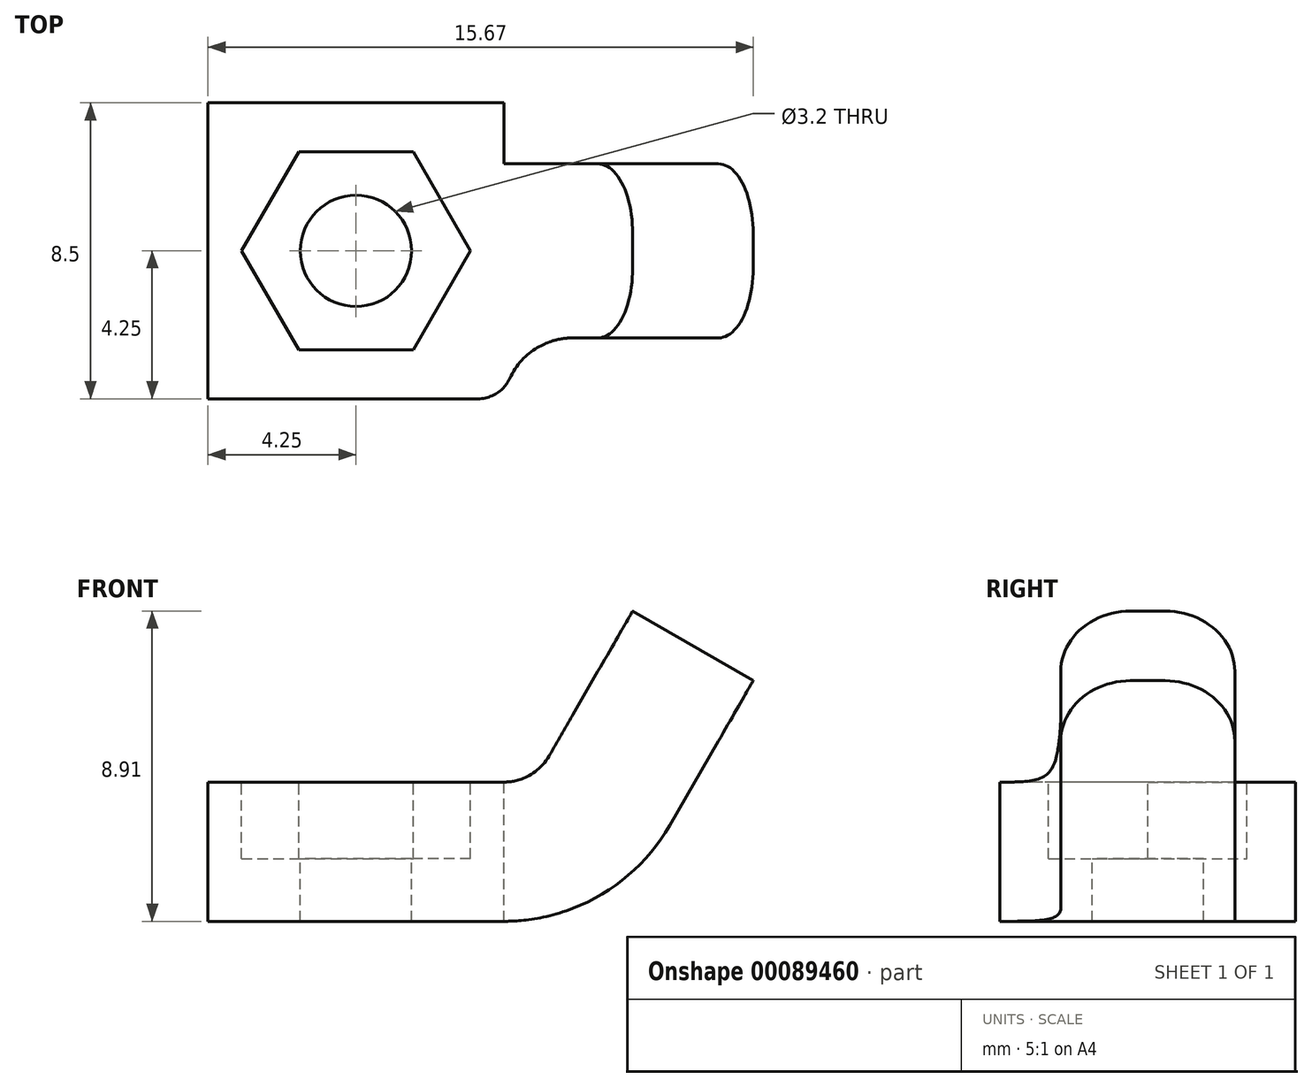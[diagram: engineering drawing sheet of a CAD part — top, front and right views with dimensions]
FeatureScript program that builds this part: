
annotation { "Feature Type Name" : "Feature", "Feature Type Description" : "" }
export const myFeature = defineFeature(function(context is Context, id is Id, definition is map)
    precondition{}
    {
        {
            var Q0;
            Q0=qCreatedBy(makeId("Top.planeOp"),FACE);
            var sketch = newSketch(context, id + "F0", { "sketchPlane" : qUnion([Q0])});
            skLineSegment(sketch, "E0.bottom", {"start": v(4.25, 4.25) * mm, "end": v(-4.25, 4.25) * mm});
            skLineSegment(sketch, "E0.top", {"start": v(4.25, -4.25) * mm, "end": v(-4.25, -4.25) * mm});
            skLineSegment(sketch, "E0.left", {"start": v(4.25, 4.25) * mm, "end": v(4.25, -4.25) * mm});
            skLineSegment(sketch, "E0.right", {"start": v(-4.25, 4.25) * mm, "end": v(-4.25, -4.25) * mm});
            skPoint(sketch, "E1", {"position": v(0, 0) * mm});
            skPoint(sketch, "E2", {"position": v(0, 4.25) * mm});
            skPoint(sketch, "E3", {"position": v(-4.25, 0) * mm});
            skCircle(sketch, "E4.cCircle", {"center": v(0, 0) * mm, "radius": 2.75 * mm, "construction": true});
            skLineSegment(sketch, "E4.0", {"start": v(-1.59, 2.75) * mm, "end": v(1.59, 2.75) * mm});
            skLineSegment(sketch, "E4.1", {"start": v(1.59, 2.75) * mm, "end": v(3.18, 0) * mm});
            skLineSegment(sketch, "E4.2", {"start": v(3.18, 0) * mm, "end": v(1.59, -2.75) * mm});
            skLineSegment(sketch, "E4.3", {"start": v(1.59, -2.75) * mm, "end": v(-1.59, -2.75) * mm});
            skLineSegment(sketch, "E4.4", {"start": v(-1.59, -2.75) * mm, "end": v(-3.18, 0) * mm});
            skLineSegment(sketch, "E4.5", {"start": v(-3.18, 0) * mm, "end": v(-1.59, 2.75) * mm});
            skPoint(sketch, "E4.0.midPoint", {"position": v(0, 2.75) * mm});
            skSolve(sketch);
        }
        {
            var Q0;
            Q0=qSketchRegion(id+"F0",true);
            var Q1;
            Q1=makeQuery(id+"F0.imprint","IMPRINT",FACE,{"disambiguationData":[TD([[makeQuery(id+"F0.imprint","IMPRINT",EDGE,{"derivedFrom":sQuery(id+"F0.wireOp",EDGE,"9c3ea140-8654-4120-b5e6-7aedb879b978.0")}),-1.0]])]});
            var Q2;
            Q2=makeQuery(id+"F0.imprint","IMPRINT",FACE,{"disambiguationData":[TD([[makeQuery(id+"F0.imprint","IMPRINT",EDGE,{"derivedFrom":sQuery(id+"F0.wireOp",EDGE,"E4.0")}),-1.0]])]});
            extrude(context, id + "F1", {"entities" : qUnion([Q0, Q1, Q2]), "depth" : 4 * mm});
        }
        {
            var Q0;
            Q0=makeQuery(id+"F1.opExtrude","CAP_FACE",FACE,{"disambiguationData":[OSD([sQuery(id+"F0.wireOp",EDGE,"E0.bottom"),sQuery(id+"F0.wireOp",EDGE,"E0.top"),sQuery(id+"F0.wireOp",EDGE,"E0.left"),sQuery(id+"F0.wireOp",EDGE,"E0.right")])],"isStart":false});
            var sketch = newSketch(context, id + "F2", { "sketchPlane" : qUnion([Q0])});
            skCircle(sketch, "E5.cCircle", {"center": v(0, 0) * mm, "radius": 2.85 * mm, "construction": true});
            skLineSegment(sketch, "E5.0", {"start": v(-1.65, 2.85) * mm, "end": v(1.65, 2.85) * mm});
            skLineSegment(sketch, "E5.1", {"start": v(1.65, 2.85) * mm, "end": v(3.3, 0) * mm});
            skLineSegment(sketch, "E5.2", {"start": v(3.3, 0) * mm, "end": v(1.65, -2.85) * mm});
            skLineSegment(sketch, "E5.3", {"start": v(1.65, -2.85) * mm, "end": v(-1.65, -2.85) * mm});
            skLineSegment(sketch, "E5.4", {"start": v(-1.65, -2.85) * mm, "end": v(-3.3, 0) * mm});
            skLineSegment(sketch, "E5.5", {"start": v(-3.3, 0) * mm, "end": v(-1.65, 2.85) * mm});
            skPoint(sketch, "E5.0.midPoint", {"position": v(0, 2.85) * mm});
            skSolve(sketch);
        }
        {
            var Q0;
            Q0 = qSketchRegion(id + "F2", true);
            extrude(context, id + "F3", {"entities" : qUnion([Q0]), "operationType" : NewBodyOperationType.REMOVE, "oppositeDirection" : true, "depth" : 2.2 * mm});
        }
        {
            var Q0;
            Q0=makeQuery(id+"F3.boolean.opBoolean","COPY",FACE,{"derivedFrom":makeQuery(id+"F3.opExtrude","CAP_FACE",FACE,{"disambiguationData":[OSD([sQuery(id+"F2.wireOp",EDGE,"E5.0"),sQuery(id+"F2.wireOp",EDGE,"E5.1"),sQuery(id+"F2.wireOp",EDGE,"E5.2"),sQuery(id+"F2.wireOp",EDGE,"E5.3"),sQuery(id+"F2.wireOp",EDGE,"E5.4"),sQuery(id+"F2.wireOp",EDGE,"E5.5")])],"isStart":false})});
            var sketch = newSketch(context, id + "F4", { "sketchPlane" : qUnion([Q0])});
            skCircle(sketch, "E6", {"center": v(0, 0) * mm, "radius": 1.6 * mm});
            skSolve(sketch);
        }
        {
            var Q0;
            Q0 = qSketchRegion(id + "F4", true);
            extrude(context, id + "F5", {"entities" : qUnion([Q0]), "operationType" : NewBodyOperationType.REMOVE, "endBound" : BoundingType.THROUGH_ALL, "oppositeDirection" : true, "depth" : 25 * mm});
        }
        {
            var Q0;
            Q0=qCreatedBy(makeId("Front.planeOp"),FACE);
            var sketch = newSketch(context, id + "F6", { "sketchPlane" : qUnion([Q0])});
            skLineSegment(sketch, "E7", {"start": v(0, 0) * mm, "end": v(0, 5) * mm});
            skLineSegment(sketch, "E8", {"start": v(0, 2.5) * mm, "end": v(4.25, 2.5) * mm});
            skLineSegment(sketch, "E9", {"start": v(6.85, 4) * mm, "end": v(9.25, 8.16) * mm});
            skPoint(sketch, "E10.visualSharp", {"position": v(5.98, 2.5) * mm});
            skArc(sketch, "E10.filletArc", {"start": v(4.25, 2.5) * mm, "mid": v(5.75, 2.9) * mm, "end": v(6.85, 4) * mm});
            skArc(sketch, "E11.MirrorCS", {"start": v(-4.25, 2.5) * mm, "mid": v(-5.75, 2.9) * mm, "end": v(-6.85, 4) * mm});
            skLineSegment(sketch, "E12.MirrorCS", {"start": v(-6.85, 4) * mm, "end": v(-9.25, 8.16) * mm});
            skSolve(sketch);
        }
        {
            var Q0;
            Q0=makeQuery(id+"F1.opExtrude","SWEPT_FACE",FACE,{"disambiguationData":[OSD([sQuery(id+"F0.wireOp",EDGE,"E0.left")])]});
            var sketch = newSketch(context, id + "F7", { "sketchPlane" : qUnion([Q0])});
            skLineSegment(sketch, "E13.bottom", {"start": v(-2.5, 0) * mm, "end": v(2.5, 0) * mm});
            skLineSegment(sketch, "E13.top", {"start": v(-2.5, 4) * mm, "end": v(2.5, 4) * mm});
            skLineSegment(sketch, "E13.left", {"start": v(-2.5, 0) * mm, "end": v(-2.5, 4) * mm});
            skLineSegment(sketch, "E13.right", {"start": v(2.5, 0) * mm, "end": v(2.5, 4) * mm});
            skPoint(sketch, "E14", {"position": v(0, 0) * mm});
            skSolve(sketch);
        }
        {
            var Q0;
            Q0=makeQuery(id+"F7.imprint","IMPRINT",FACE,{"disambiguationData":[TD([[makeQuery(id+"F7.imprint","IMPRINT",EDGE,{"derivedFrom":sQuery(id+"F7.wireOp",EDGE,"E13.bottom")}),-1.0]])]});
            var Q1;
            Q1=sQuery(id+"F6.wireOp",EDGE,"E10.filletArc");
            var Q2;
            Q2=sQuery(id+"F6.wireOp",EDGE,"E9");
            sweep(context, id + "F8", {"operationType" : NewBodyOperationType.ADD, "profiles" : qUnion([Q0]), "path" : qUnion([Q1, Q2])});
        }
        {
            var Q0;
            Q0=makeQuery(id+"F8.opSweep","CAP_EDGE",EDGE,{"disambiguationData":[OSD([sQuery(id+"F6.wireOp",VERTEX,"E10.filletArc.start"),sQuery(id+"F7.wireOp",EDGE,"E13.left")])],"isStart":true});
            var Q1;
            Q1=makeQuery(id+"FKS6proBDLbqMdM_1.1.F8.opSweep","CAP_EDGE",EDGE,{"disambiguationData":[OSD([sQuery(id+"F6.wireOp",VERTEX,"E10.filletArc.start"),sQuery(id+"F7.wireOp",EDGE,"E13.right")])],"isStart":true});
            var Q2;
            Q2=makeQuery(id+"FKS6proBDLbqMdM_1.1.F8.opSweep","CAP_EDGE",EDGE,{"disambiguationData":[OSD([sQuery(id+"F6.wireOp",VERTEX,"E10.filletArc.start"),sQuery(id+"F7.wireOp",EDGE,"E13.left")])],"isStart":true});
            var Q3;
            Q3=makeQuery(id+"F8.opSweep","CAP_EDGE",EDGE,{"disambiguationData":[OSD([sQuery(id+"F6.wireOp",VERTEX,"E10.filletArc.start"),sQuery(id+"F7.wireOp",EDGE,"E13.right")])],"isStart":true});
            fillet(context, id + "F9", {"entities" : qUnion([Q0, Q1, Q2, Q3]), "radius" : 2 * mm, "tangentPropagation" : true, "allowEdgeOverflow" : false});
        }
        {
            var Q0;
            Q0=makeQuery(id+"FKS6proBDLbqMdM_1.1.F8.opSweep","CAP_EDGE",EDGE,{"disambiguationData":[OSD([sQuery(id+"F6.wireOp",VERTEX,"E9.end"),sQuery(id+"F7.wireOp",EDGE,"E13.left")])],"isStart":false});
            var Q1;
            Q1=makeQuery(id+"FKS6proBDLbqMdM_1.1.F8.opSweep","CAP_EDGE",EDGE,{"disambiguationData":[OSD([sQuery(id+"F6.wireOp",VERTEX,"E9.end"),sQuery(id+"F7.wireOp",EDGE,"E13.right")])],"isStart":false});
            var Q2;
            Q2=makeQuery(id+"F8.opSweep","CAP_EDGE",EDGE,{"disambiguationData":[OSD([sQuery(id+"F6.wireOp",VERTEX,"E9.end"),sQuery(id+"F7.wireOp",EDGE,"E13.right")])],"isStart":false});
            var Q3;
            Q3=makeQuery(id+"F8.opSweep","CAP_EDGE",EDGE,{"disambiguationData":[OSD([sQuery(id+"F6.wireOp",VERTEX,"E9.end"),sQuery(id+"F7.wireOp",EDGE,"E13.left")])],"isStart":false});
            fillet(context, id + "F10", {"entities" : qUnion([Q0, Q1, Q2, Q3]), "radius" : 2 * mm, "tangentPropagation" : true, "allowEdgeOverflow" : false});
        }
        {
            var Q0;
            Q0=makeQuery(id+"F9.opFillet","BLEND_EDGE",EDGE,{"blendedFrom":[makeQuery(id+"FKS6proBDLbqMdM_1.1.F8.opSweep","CAP_EDGE",EDGE,{"disambiguationData":[OSD([sQuery(id+"F6.wireOp",VERTEX,"E10.filletArc.start"),sQuery(id+"F7.wireOp",EDGE,"E13.left")])],"isStart":true}),makeQuery(id+"F1.opExtrude","SWEPT_FACE",FACE,{"disambiguationData":[OSD([sQuery(id+"F0.wireOp",EDGE,"E0.bottom")])]})],"blendedInto":[makeQuery(id+"F1.opExtrude","SWEPT_FACE",FACE,{"disambiguationData":[OSD([sQuery(id+"F0.wireOp",EDGE,"E0.bottom")])]})]});
            var Q1;
            Q1=makeQuery(id+"F9.opFillet","BLEND_EDGE",EDGE,{"blendedFrom":[makeQuery(id+"F8.opSweep","CAP_EDGE",EDGE,{"disambiguationData":[OSD([sQuery(id+"F6.wireOp",VERTEX,"E10.filletArc.start"),sQuery(id+"F7.wireOp",EDGE,"E13.right")])],"isStart":true}),makeQuery(id+"F1.opExtrude","SWEPT_FACE",FACE,{"disambiguationData":[OSD([sQuery(id+"F0.wireOp",EDGE,"E0.bottom")])]})],"blendedInto":[makeQuery(id+"F1.opExtrude","SWEPT_FACE",FACE,{"disambiguationData":[OSD([sQuery(id+"F0.wireOp",EDGE,"E0.bottom")])]})]});
            var Q2;
            Q2=makeQuery(id+"F9.opFillet","BLEND_EDGE",EDGE,{"blendedFrom":[makeQuery(id+"F8.opSweep","CAP_EDGE",EDGE,{"disambiguationData":[OSD([sQuery(id+"F6.wireOp",VERTEX,"E10.filletArc.start"),sQuery(id+"F7.wireOp",EDGE,"E13.left")])],"isStart":true}),makeQuery(id+"F1.opExtrude","SWEPT_FACE",FACE,{"disambiguationData":[OSD([sQuery(id+"F0.wireOp",EDGE,"E0.top")])]})],"blendedInto":[makeQuery(id+"F1.opExtrude","SWEPT_FACE",FACE,{"disambiguationData":[OSD([sQuery(id+"F0.wireOp",EDGE,"E0.top")])]})]});
            var Q3;
            Q3=makeQuery(id+"F9.opFillet","BLEND_EDGE",EDGE,{"blendedFrom":[makeQuery(id+"FKS6proBDLbqMdM_1.1.F8.opSweep","CAP_EDGE",EDGE,{"disambiguationData":[OSD([sQuery(id+"F6.wireOp",VERTEX,"E10.filletArc.start"),sQuery(id+"F7.wireOp",EDGE,"E13.right")])],"isStart":true}),makeQuery(id+"F1.opExtrude","SWEPT_FACE",FACE,{"disambiguationData":[OSD([sQuery(id+"F0.wireOp",EDGE,"E0.top")])]})],"blendedInto":[makeQuery(id+"F1.opExtrude","SWEPT_FACE",FACE,{"disambiguationData":[OSD([sQuery(id+"F0.wireOp",EDGE,"E0.top")])]})]});
            fillet(context, id + "F11", {"entities" : qUnion([Q0, Q1, Q2, Q3]), "radius" : 1 * mm, "tangentPropagation" : true, "allowEdgeOverflow" : false});
        }
    });
